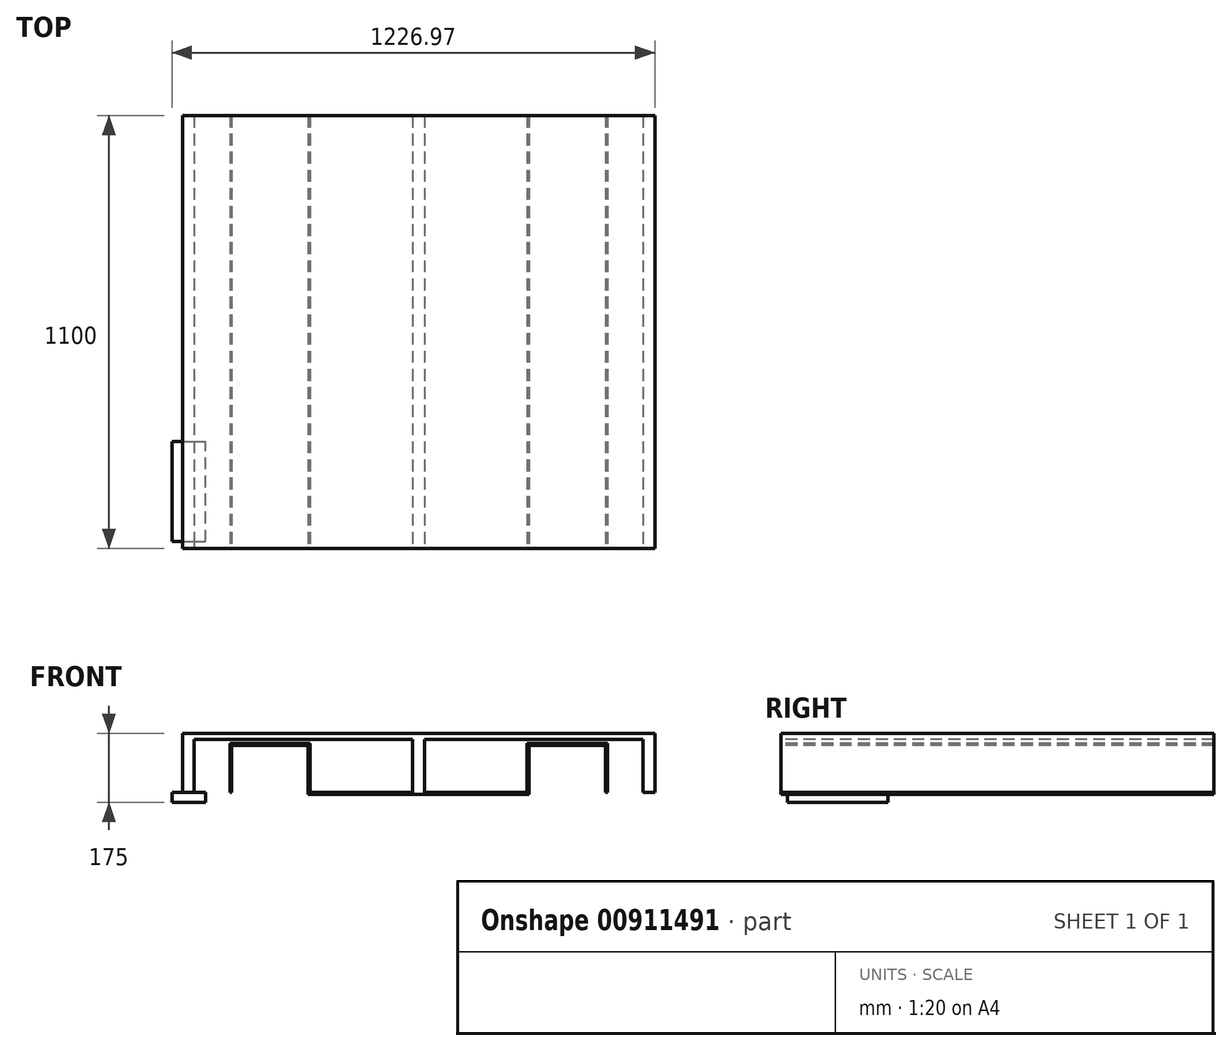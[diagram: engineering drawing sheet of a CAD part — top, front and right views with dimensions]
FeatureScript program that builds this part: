
annotation { "Feature Type Name" : "Feature", "Feature Type Description" : "" }
export const myFeature = defineFeature(function(context is Context, id is Id, definition is map)
    precondition{}
    {
        {
            var Q0;
            Q0=qCreatedBy(makeId("Front.planeOp"),FACE);
            var sketch = newSketch(context, id + "F0", { "sketchPlane" : qUnion([Q0])});
            skLineSegment(sketch, "E0", {"start": v(0, 150) * mm, "end": v(600, 150) * mm});
            skLineSegment(sketch, "E1", {"start": v(600, 150) * mm, "end": v(600, 0) * mm});
            skLineSegment(sketch, "E2", {"start": v(600, 0) * mm, "end": v(570, 0) * mm});
            skLineSegment(sketch, "E3", {"start": v(570, 0) * mm, "end": v(570, 135) * mm});
            skLineSegment(sketch, "E4", {"start": v(570, 135) * mm, "end": v(15, 135) * mm});
            skLineSegment(sketch, "E5", {"start": v(15, 135) * mm, "end": v(15, 0) * mm});
            skLineSegment(sketch, "E6", {"start": v(15, 0) * mm, "end": v(0, 0) * mm});
            skLineSegment(sketch, "E7", {"start": v(0, 0) * mm, "end": v(0, 150) * mm});
            skLineSegment(sketch, "E8.MirrorCS", {"start": v(-600, 0) * mm, "end": v(-570, 0) * mm});
            skLineSegment(sketch, "E9.MirrorCS", {"start": v(-15, 0) * mm, "end": v(0, 0) * mm});
            skLineSegment(sketch, "E10.MirrorCS", {"start": v(-570, 0) * mm, "end": v(-570, 135) * mm});
            skLineSegment(sketch, "E11.MirrorCS", {"start": v(0, 150) * mm, "end": v(-600, 150) * mm});
            skLineSegment(sketch, "E12.MirrorCS", {"start": v(-600, 150) * mm, "end": v(-600, 0) * mm});
            skLineSegment(sketch, "E13.MirrorCS", {"start": v(-15, 135) * mm, "end": v(-15, 0) * mm});
            skLineSegment(sketch, "E14.MirrorCS", {"start": v(-570, 135) * mm, "end": v(-15, 135) * mm});
            skSolve(sketch);
        }
        {
            var Q0;
            Q0=makeQuery(id+"F0.imprint","IMPRINT",FACE,{"disambiguationData":[TD([[makeQuery(id+"F0.imprint","IMPRINT",EDGE,{"derivedFrom":sQuery(id+"F0.wireOp",EDGE,"E0")}),-1.0]])]});
            var Q1;
            Q1=makeQuery(id+"F0.imprint","IMPRINT",FACE,{"disambiguationData":[TD([[makeQuery(id+"F0.imprint","IMPRINT",EDGE,{"derivedFrom":sQuery(id+"F0.wireOp",EDGE,"E7")}),1.0]])]});
            extrude(context, id + "F1", {"entities" : qUnion([Q0, Q1]), "oppositeDirection" : true, "depth" : 1100 * mm, "offsetDistance" : 25 * mm});
        }
        {
            var Q0;
            Q0=qCreatedBy(makeId("Front.planeOp"),FACE);
            var sketch = newSketch(context, id + "F2", { "sketchPlane" : qUnion([Q0])});
            skLineSegment(sketch, "E15", {"start": v(479.57, 0) * mm, "end": v(479.57, 125.2) * mm});
            skLineSegment(sketch, "E16", {"start": v(479.57, 125.2) * mm, "end": v(275.86, 125.2) * mm});
            skLineSegment(sketch, "E17", {"start": v(275.86, 125.2) * mm, "end": v(275.86, 0) * mm});
            skLineSegment(sketch, "E18", {"start": v(275.86, 0) * mm, "end": v(0, 0) * mm});
            skLineSegment(sketch, "E19.0", {"start": v(280.86, -5) * mm, "end": v(0, -5) * mm});
            skLineSegment(sketch, "E19.1", {"start": v(280.86, 120.2) * mm, "end": v(280.86, -5) * mm});
            skLineSegment(sketch, "E19.2", {"start": v(474.57, 120.2) * mm, "end": v(280.86, 120.2) * mm});
            skLineSegment(sketch, "E19.3", {"start": v(474.57, 0) * mm, "end": v(474.57, 120.2) * mm});
            skLineSegment(sketch, "E20", {"start": v(479.57, 0) * mm, "end": v(474.57, 0) * mm});
            skLineSegment(sketch, "E21", {"start": v(0, 0) * mm, "end": v(0, -5) * mm});
            skLineSegment(sketch, "E22.MirrorCS", {"start": v(-275.86, 125.2) * mm, "end": v(-275.86, 0) * mm});
            skLineSegment(sketch, "E23.MirrorCS", {"start": v(-280.86, 120.2) * mm, "end": v(-280.86, -5) * mm});
            skLineSegment(sketch, "E24.MirrorCS", {"start": v(-479.57, 0) * mm, "end": v(-474.57, 0) * mm});
            skLineSegment(sketch, "E25.MirrorCS", {"start": v(-280.86, -5) * mm, "end": v(0, -5) * mm});
            skLineSegment(sketch, "E26.MirrorCS", {"start": v(-275.86, 0) * mm, "end": v(0, 0) * mm});
            skLineSegment(sketch, "E27.MirrorCS", {"start": v(-479.57, 125.2) * mm, "end": v(-275.86, 125.2) * mm});
            skLineSegment(sketch, "E28.MirrorCS", {"start": v(-474.57, 120.2) * mm, "end": v(-280.86, 120.2) * mm});
            skLineSegment(sketch, "E29.MirrorCS", {"start": v(-479.57, 0) * mm, "end": v(-479.57, 125.2) * mm});
            skLineSegment(sketch, "E30.MirrorCS", {"start": v(-474.57, 0) * mm, "end": v(-474.57, 120.2) * mm});
            skSolve(sketch);
        }
        {
            var Q0;
            Q0=makeQuery(id+"F2.imprint","IMPRINT",FACE,{"disambiguationData":[TD([[makeQuery(id+"F2.imprint","IMPRINT",EDGE,{"derivedFrom":sQuery(id+"F2.wireOp",EDGE,"E21")}),-1.0]])]});
            var Q1;
            Q1=makeQuery(id+"F2.imprint","IMPRINT",FACE,{"disambiguationData":[TD([[makeQuery(id+"F2.imprint","IMPRINT",EDGE,{"derivedFrom":sQuery(id+"F2.wireOp",EDGE,"E15")}),1.0]])]});
            extrude(context, id + "F3", {"entities" : qUnion([Q0, Q1]), "operationType" : NewBodyOperationType.ADD, "oppositeDirection" : true, "depth" : 1100 * mm, "offsetDistance" : 25 * mm});
        }
        {
            var Q0;
            Q0=makeQuery(id+"F1.opExtrude","SWEPT_FACE",FACE,{"disambiguationData":[OSD([sQuery(id+"F0.wireOp",EDGE,"E8.MirrorCS")])]});
            var sketch = newSketch(context, id + "F4", { "sketchPlane" : qUnion([Q0])});
            skLineSegment(sketch, "E31.bottom", {"start": v(-626.97, -17.53) * mm, "end": v(-541, -17.53) * mm});
            skLineSegment(sketch, "E31.top", {"start": v(-626.97, -272.23) * mm, "end": v(-541, -272.23) * mm});
            skLineSegment(sketch, "E31.left", {"start": v(-626.97, -17.53) * mm, "end": v(-626.97, -272.23) * mm});
            skLineSegment(sketch, "E31.right", {"start": v(-541, -17.53) * mm, "end": v(-541, -272.23) * mm});
            skSolve(sketch);
        }
        {
            var Q0;
            Q0 = qSketchRegion(id + "F4", true);
            extrude(context, id + "F5", {"entities" : qUnion([Q0]), "operationType" : NewBodyOperationType.ADD, "depth" : 25 * mm, "offsetDistance" : 25 * mm});
        }
    });
